# Revit family: MADEL_DAMPER_FIRE PROTECTION_FOK-EIS-120
name_source: partatom
category: Accesorios de conductos
revit_build: Autodesk Revit 2015 (Build: 20140606_1530(x64)
units: mm (PartAtom-declared; Revit-internal decimal feet)

## types (1)
- MADEL_DAMPER_FIRE PROTECTION_FOK-EIS-120
    Afree = 0.1974 m²
    BIMETRICAL = http://www.bimetrical.com
    BIMETRICAL Category = Damper
    Comentarios de tipo = Fire dampers for rectangular duct mounting. Dampers for horizontal assembly, tested and classed EIS-120 (Integrity, Insulation and smoke leakage during 120 minutes in accordance to the European standard EN-1366-2, to comply with building regulations for fire safety. Dampers with shutting mechanism by thermal fusible link at 72ºC. An expanding joint together an air-tightness joint, as much prevent the propagation of smoke to high as to low temperature.
    Descripción = MADEL_Dampers classed EIS-120 with external filler
    Fabricante = MADEL
    Family Version = 1.0
    H = 500 mm  [stored 1.64042 ft]
    IfcExportAs = IfcDamperType
    IfcExportType = IfcDamperType
    Imagen de tipo = <Ninguno>
    Kf = -4.180339
    Kr = 0.495189
    L = 500 mm  [stored 1.64042 ft]
    Material Damper = <Por categoría>
    Modelo = FOK-EIS-120-H 500x500
    Product Size = 500x500
    Q max = 5,685 m³/h
    Q min = 711 m³/h
    Review Date = 11/2016
    Revit Version = Revit 2015 - English
    Standard = UNE-EN 1366-2 / UNE-EN 13501-3
    URL = http://www.madel.com
    Vmax = 8.0 m/s
    Vmed = 4.5 m/s
    Vmin = 1.0 m/s
    b_factor = -0.349
    c_factor = 4.9567
    m_factor = 2.16096
    n_factor = 26.481

note: [stored X ft] marks values corroborated as IEEE doubles in the binary element streams (Revit-internal decimal feet)

## geometry (parser evidence)
native form markers: Blend x4
no freeform markers — native parametric forms only
